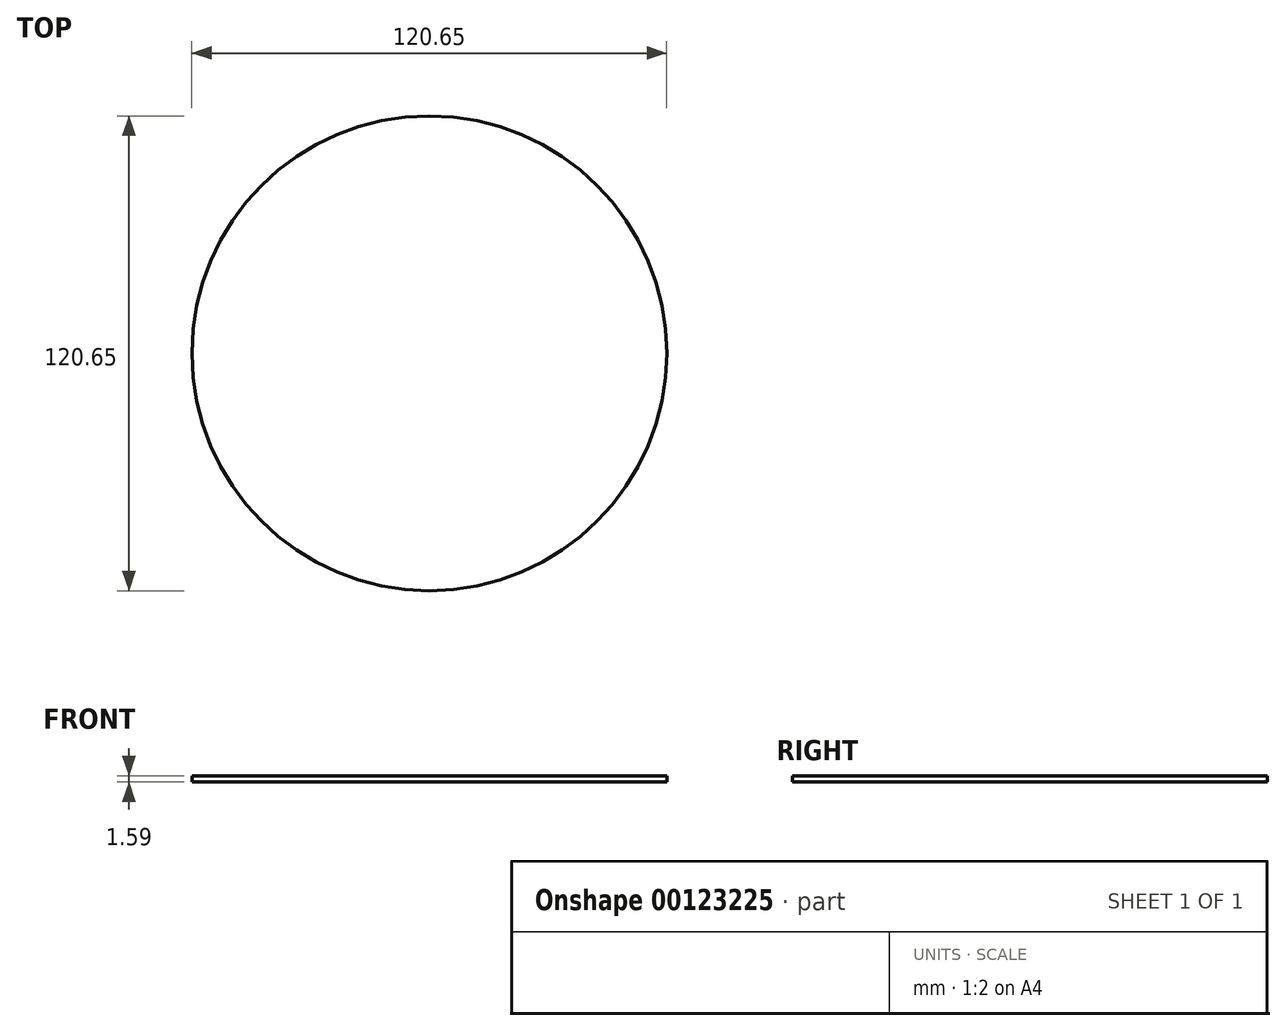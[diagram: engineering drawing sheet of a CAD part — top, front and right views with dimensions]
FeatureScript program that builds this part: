
annotation { "Feature Type Name" : "Feature", "Feature Type Description" : "" }
export const myFeature = defineFeature(function(context is Context, id is Id, definition is map)
    precondition{}
    {
        {
            var Q0;
            Q0=qCreatedBy(makeId("Top.planeOp"),FACE);
            var sketch = newSketch(context, id + "F0", { "sketchPlane" : qUnion([Q0])});
            skCircle(sketch, "E0", {"center": v(-16.72, 18.81) * mm, "radius": 60.33 * mm});
            skSolve(sketch);
        }
        {
            var Q0;
            Q0=makeQuery(id+"F0.imprint","IMPRINT",FACE,{"disambiguationData":[TD([[makeQuery(id+"F0.imprint","IMPRINT",EDGE,{"derivedFrom":sQuery(id+"F0.wireOp",EDGE,"E0")}),1.0]])]});
            extrude(context, id + "F1", {"entities" : qUnion([Q0]), "depth" : 1.59 * mm});
        }
    });
